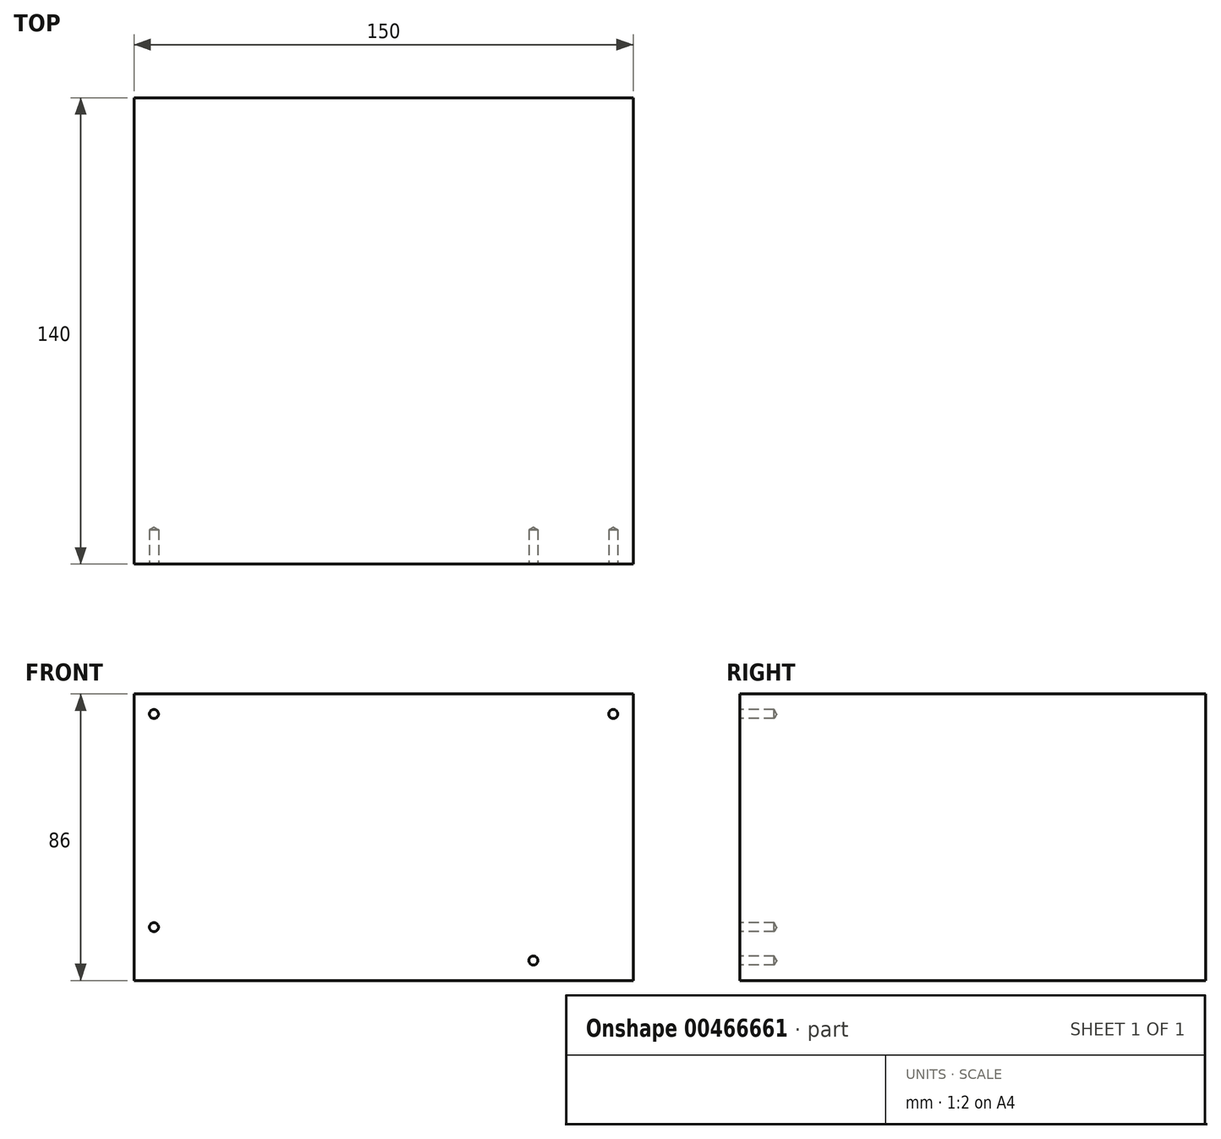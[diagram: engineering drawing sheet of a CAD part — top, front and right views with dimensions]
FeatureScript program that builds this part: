
annotation { "Feature Type Name" : "Feature", "Feature Type Description" : "" }
export const myFeature = defineFeature(function(context is Context, id is Id, definition is map)
    precondition{}
    {
        {
            var Q0;
            Q0=qCreatedBy(makeId("Front.planeOp"),FACE);
            var sketch = newSketch(context, id + "F0", { "sketchPlane" : qUnion([Q0])});
            skLineSegment(sketch, "E0.bottom", {"start": v(0, 0) * mm, "end": v(-150, 0) * mm});
            skLineSegment(sketch, "E0.top", {"start": v(0, 86) * mm, "end": v(-150, 86) * mm});
            skLineSegment(sketch, "E0.left", {"start": v(0, 0) * mm, "end": v(0, 86) * mm});
            skLineSegment(sketch, "E0.right", {"start": v(-150, 0) * mm, "end": v(-150, 86) * mm});
            skSolve(sketch);
        }
        {
            var Q0;
            Q0 = qSketchRegion(id + "F0", true);
            extrude(context, id + "F1", {"entities" : qUnion([Q0]), "depth" : 140 * mm});
        }
        {
            var Q0;
            Q0=makeQuery(id+"F1.opExtrude","CAP_FACE",FACE,{"disambiguationData":[OSD([sQuery(id+"F0.wireOp",EDGE,"E0.bottom"),sQuery(id+"F0.wireOp",EDGE,"E0.top"),sQuery(id+"F0.wireOp",EDGE,"E0.left"),sQuery(id+"F0.wireOp",EDGE,"E0.right")])],"isStart":false});
            var sketch = newSketch(context, id + "F2", { "sketchPlane" : qUnion([Q0])});
            skPoint(sketch, "E1", {"position": v(-144, 80) * mm});
            skPoint(sketch, "E2", {"position": v(-6, 80) * mm});
            skPoint(sketch, "E3", {"position": v(-144, 16) * mm});
            skPoint(sketch, "E4", {"position": v(-30, 6) * mm});
            skSolve(sketch);
        }
        {
            var Q0;
            Q0=sQuery(id+"F2.wireOp",VERTEX,"E1");
            var Q1;
            Q1=sQuery(id+"F2.wireOp",VERTEX,"E4");
            var Q2;
            Q2=sQuery(id+"F2.wireOp",VERTEX,"E2");
            var Q3;
            Q3=sQuery(id+"F2.wireOp",VERTEX,"E3");
            var Q4;
            Q4=makeQuery(id+"F1.opExtrude","SWEPT_BODY",BODY,{"disambiguationData":[OSD([sQuery(id+"F0.wireOp",EDGE,"E0.bottom"),sQuery(id+"F0.wireOp",EDGE,"E0.top"),sQuery(id+"F0.wireOp",EDGE,"E0.left"),sQuery(id+"F0.wireOp",EDGE,"E0.right")])]});
            hole(context, id + "F3", {"style" : HoleStyle.SIMPLE, "endStyle" : HoleEndStyle.BLIND, "standardTappedOrClearance" : lookupTablePath({ "standard" : "ANSI", "engagement" : "75%", "pitch" : "32 tpi", "size" : "#6", "type" : "Tapped" }), "standardBlindInLast" : lookupTablePath({ "standard" : "ANSI", "engagement" : "75%", "pitch" : "32 tpi", "size" : "#6", "type" : "Tapped" }), "holeDiameter" : 2.7 * mm, "showTappedDepth" : true, "holeDepth" : 10.3 * mm, "isTappedThrough" : true, "tappedDepth" : 6.34 * mm, "tapClearance" : 5, "locations" : qUnion([Q0, Q1, Q2, Q3]), "scope" : qUnion([Q4]), "majorDiameter" : 3.5 * mm});
        }
    });
